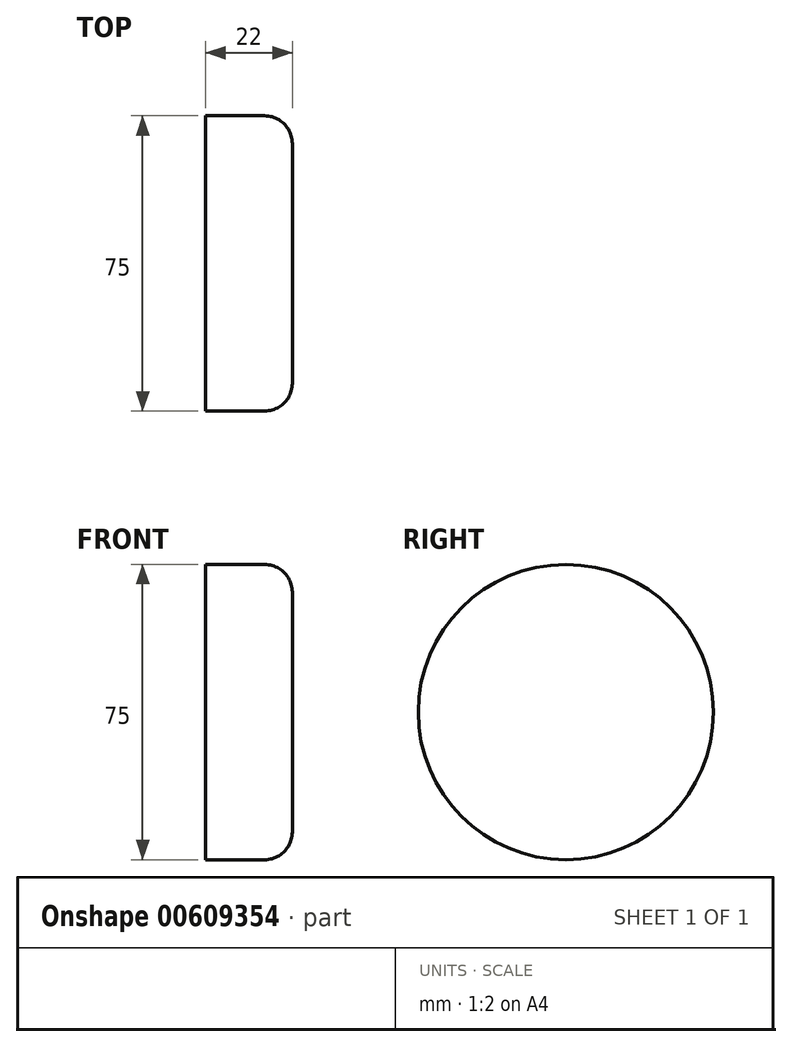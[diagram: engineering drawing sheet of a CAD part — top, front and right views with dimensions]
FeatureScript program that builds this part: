
annotation { "Feature Type Name" : "Feature", "Feature Type Description" : "" }
export const myFeature = defineFeature(function(context is Context, id is Id, definition is map)
    precondition{}
    {
        {
            var Q0;
            Q0=qCreatedBy(makeId("Right.planeOp"),FACE);
            var sketch = newSketch(context, id + "F0", { "sketchPlane" : qUnion([Q0])});
            skCircle(sketch, "E0", {"center": v(0, 0) * mm, "radius": 37.5 * mm});
            skSolve(sketch);
        }
        {
            var Q0;
            Q0 = qSketchRegion(id + "F0", true);
            extrude(context, id + "F1", {"entities" : qUnion([Q0]), "depth" : 22 * mm, "offsetDistance" : 25 * mm});
        }
        {
            var Q0;
            Q0=makeQuery(id+"F1.opExtrude","CAP_EDGE",EDGE,{"disambiguationData":[OSD([sQuery(id+"F0.wireOp",EDGE,"E0")])],"isStart":false});
            fillet(context, id + "F2", {"entities" : qUnion([Q0]), "radius" : 7 * mm, "tangentPropagation" : true, "allowEdgeOverflow" : false});
        }
    });
